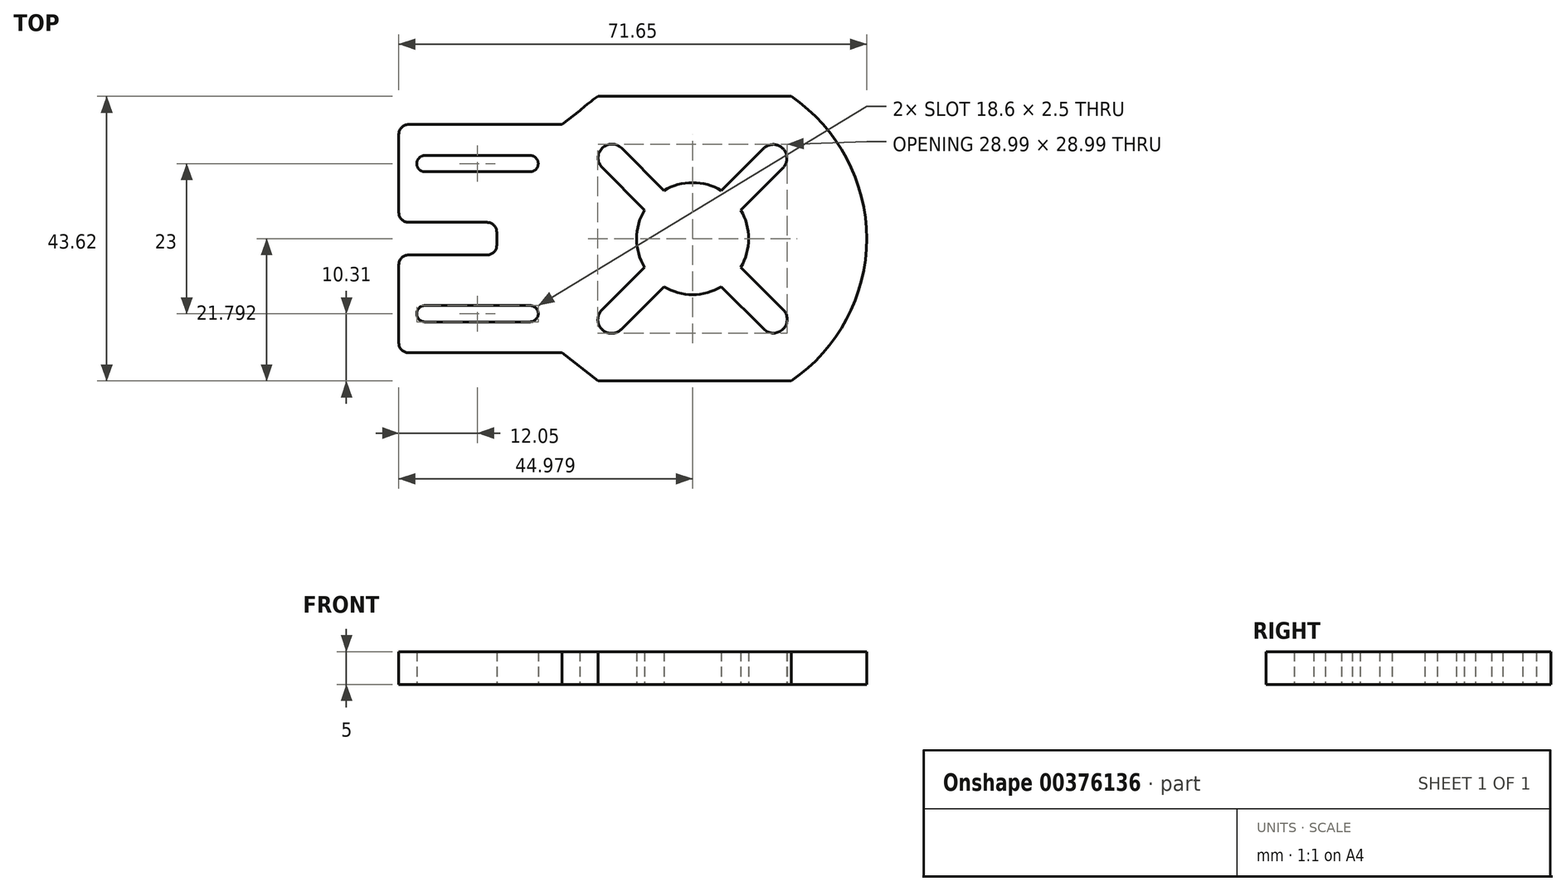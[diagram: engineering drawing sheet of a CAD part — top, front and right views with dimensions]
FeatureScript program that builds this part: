
annotation { "Feature Type Name" : "Feature", "Feature Type Description" : "" }
export const myFeature = defineFeature(function(context is Context, id is Id, definition is map)
    precondition{}
    {
        {
            var Q0;
            Q0=qCreatedBy(makeId("Top.planeOp"),FACE);
            var sketch = newSketch(context, id + "F0", { "sketchPlane" : qUnion([Q0])});
            skLineSegment(sketch, "E0.bottom", {"start": v(1.5, 0) * mm, "end": v(65, 0) * mm});
            skLineSegment(sketch, "E0.top", {"start": v(1.5, 35) * mm, "end": v(25, 35) * mm});
            skLineSegment(sketch, "E0.left", {"start": v(0, 1.5) * mm, "end": v(0, 13.5) * mm});
            skPoint(sketch, "E1.orphan", {"position": v(0, 17.5) * mm});
            skArc(sketch, "E2", {"start": v(34.11, 31.36) * mm, "mid": v(31.14, 31.36) * mm, "end": v(31.14, 28.4) * mm});
            skPoint(sketch, "E3.center.orphan", {"position": v(4, 29) * mm});
            skPoint(sketch, "E4.center.orphan", {"position": v(20.1, 29) * mm});
            skPoint(sketch, "E5.visualSharp", {"position": v(0, 35) * mm});
            skArc(sketch, "E5.filletArc", {"start": v(1.5, 35) * mm, "mid": v(0.44, 34.56) * mm, "end": v(0, 33.5) * mm});
            skPoint(sketch, "E6.visualSharp", {"position": v(0, 0) * mm});
            skArc(sketch, "E6.filletArc", {"start": v(0, 1.5) * mm, "mid": v(0.44, 0.44) * mm, "end": v(1.5, 0) * mm});
            skPoint(sketch, "E7.MirrorP", {"position": v(4, 6) * mm});
            skArc(sketch, "E8.MirrorCS", {"start": v(20.1, 7.25) * mm, "mid": v(21.35, 6) * mm, "end": v(20.1, 4.75) * mm});
            skLineSegment(sketch, "E9", {"start": v(1.5, 20) * mm, "end": v(13.5, 20) * mm});
            skLineSegment(sketch, "E10", {"start": v(15, 18.5) * mm, "end": v(15, 16.5) * mm});
            skLineSegment(sketch, "E11", {"start": v(13.5, 15) * mm, "end": v(1.5, 15) * mm});
            skLineSegment(sketch, "E12.trimOffspring", {"start": v(0, 21.5) * mm, "end": v(0, 33.5) * mm});
            skPoint(sketch, "E13.visualSharp", {"position": v(0, 20) * mm});
            skArc(sketch, "E13.filletArc", {"start": v(0, 21.5) * mm, "mid": v(0.44, 20.44) * mm, "end": v(1.5, 20) * mm});
            skPoint(sketch, "E14.visualSharp", {"position": v(0, 15) * mm});
            skArc(sketch, "E14.filletArc", {"start": v(1.5, 15) * mm, "mid": v(0.44, 14.56) * mm, "end": v(0, 13.5) * mm});
            skPoint(sketch, "E15.visualSharp", {"position": v(15, 20) * mm});
            skArc(sketch, "E15.filletArc", {"start": v(15, 18.5) * mm, "mid": v(14.56, 19.56) * mm, "end": v(13.5, 20) * mm});
            skPoint(sketch, "E16.visualSharp", {"position": v(15, 15) * mm});
            skArc(sketch, "E16.filletArc", {"start": v(13.5, 15) * mm, "mid": v(14.56, 15.44) * mm, "end": v(15, 16.5) * mm});
            skLineSegment(sketch, "E17", {"start": v(31.14, 28.4) * mm, "end": v(37.63, 21.9) * mm});
            skLineSegment(sketch, "E18", {"start": v(34.11, 31.36) * mm, "end": v(40.6, 24.87) * mm});
            skLineSegment(sketch, "E19", {"start": v(4, 7.25) * mm, "end": v(20.1, 7.25) * mm});
            skLineSegment(sketch, "E20", {"start": v(4, 4.75) * mm, "end": v(20.1, 4.75) * mm});
            skArc(sketch, "E21", {"start": v(4, 7.25) * mm, "mid": v(2.75, 6) * mm, "end": v(4, 4.75) * mm});
            skArc(sketch, "E22", {"start": v(4, 30.25) * mm, "mid": v(2.75, 29) * mm, "end": v(4, 27.75) * mm});
            skArc(sketch, "E23", {"start": v(20.1, 27.75) * mm, "mid": v(21.35, 29) * mm, "end": v(20.1, 30.25) * mm});
            skLineSegment(sketch, "E24", {"start": v(4, 27.75) * mm, "end": v(20.1, 27.75) * mm});
            skLineSegment(sketch, "E25", {"start": v(20.1, 30.25) * mm, "end": v(4, 30.25) * mm});
            skArc(sketch, "E26", {"start": v(37.63, 21.9) * mm, "mid": v(36.42, 17.5) * mm, "end": v(37.63, 13.1) * mm});
            skPoint(sketch, "E27.trimOffspring.center.orphan", {"position": v(44.92, 17.5) * mm});
            skArc(sketch, "E28.trimOffspring", {"start": v(49.4, 24.87) * mm, "mid": v(45, 26.08) * mm, "end": v(40.6, 24.87) * mm});
            skArc(sketch, "E29.trimOffspring", {"start": v(52.37, 13.1) * mm, "mid": v(53.58, 17.5) * mm, "end": v(52.37, 21.9) * mm});
            skArc(sketch, "E30.trimOffspring", {"start": v(40.6, 10.13) * mm, "mid": v(45, 8.92) * mm, "end": v(49.4, 10.13) * mm});
            skLineSegment(sketch, "E31", {"start": v(45, 17.5) * mm, "end": v(57.37, 5.12) * mm});
            skArc(sketch, "E32", {"start": v(58.82, 28.35) * mm, "mid": v(58.82, 31.32) * mm, "end": v(55.85, 31.32) * mm});
            skLineSegment(sketch, "E33", {"start": v(55.85, 31.32) * mm, "end": v(49.4, 24.87) * mm});
            skLineSegment(sketch, "E34", {"start": v(58.82, 28.35) * mm, "end": v(52.37, 21.9) * mm});
            skArc(sketch, "E35", {"start": v(31.1, 6.57) * mm, "mid": v(31.1, 3.6) * mm, "end": v(34.07, 3.6) * mm});
            skLineSegment(sketch, "E36", {"start": v(31.1, 6.57) * mm, "end": v(37.63, 13.1) * mm});
            skLineSegment(sketch, "E37", {"start": v(34.07, 3.6) * mm, "end": v(40.6, 10.13) * mm});
            skArc(sketch, "E38", {"start": v(55.89, 3.64) * mm, "mid": v(58.86, 3.64) * mm, "end": v(58.86, 6.6) * mm});
            skLineSegment(sketch, "E39", {"start": v(58.86, 6.6) * mm, "end": v(52.37, 13.1) * mm});
            skLineSegment(sketch, "E40", {"start": v(55.89, 3.64) * mm, "end": v(49.4, 10.13) * mm});
            skArc(sketch, "E41", {"start": v(60.08, -4.31) * mm, "mid": v(71.65, 17.5) * mm, "end": v(60.08, 39.31) * mm});
            skLineSegment(sketch, "E42", {"start": v(25, 35) * mm, "end": v(30.52, 39.31) * mm});
            skLineSegment(sketch, "E43", {"start": v(45, 17.5) * mm, "end": v(18.64, 17.5) * mm});
            skLineSegment(sketch, "E44", {"start": v(30.52, 39.31) * mm, "end": v(60.08, 39.31) * mm});
            skArc(sketch, "E45.trimOffspring", {"start": v(30.52, 39.31) * mm, "mid": v(29.07, 38.26) * mm, "end": v(27.7, 37.1) * mm});
            skLineSegment(sketch, "E46.MirrorCS", {"start": v(30.52, -4.31) * mm, "end": v(60.08, -4.31) * mm});
            skLineSegment(sketch, "E47.MirrorCS", {"start": v(25, 0) * mm, "end": v(30.52, -4.31) * mm});
            skPoint(sketch, "E48.orphan", {"position": v(65, 35) * mm});
            skSolve(sketch);
        }
        {
            var Q0;
            Q0 = qSketchRegion(id + "F0", true);
            extrude(context, id + "F1", {"entities" : qUnion([Q0]), "depth" : 5 * mm});
        }
    });
